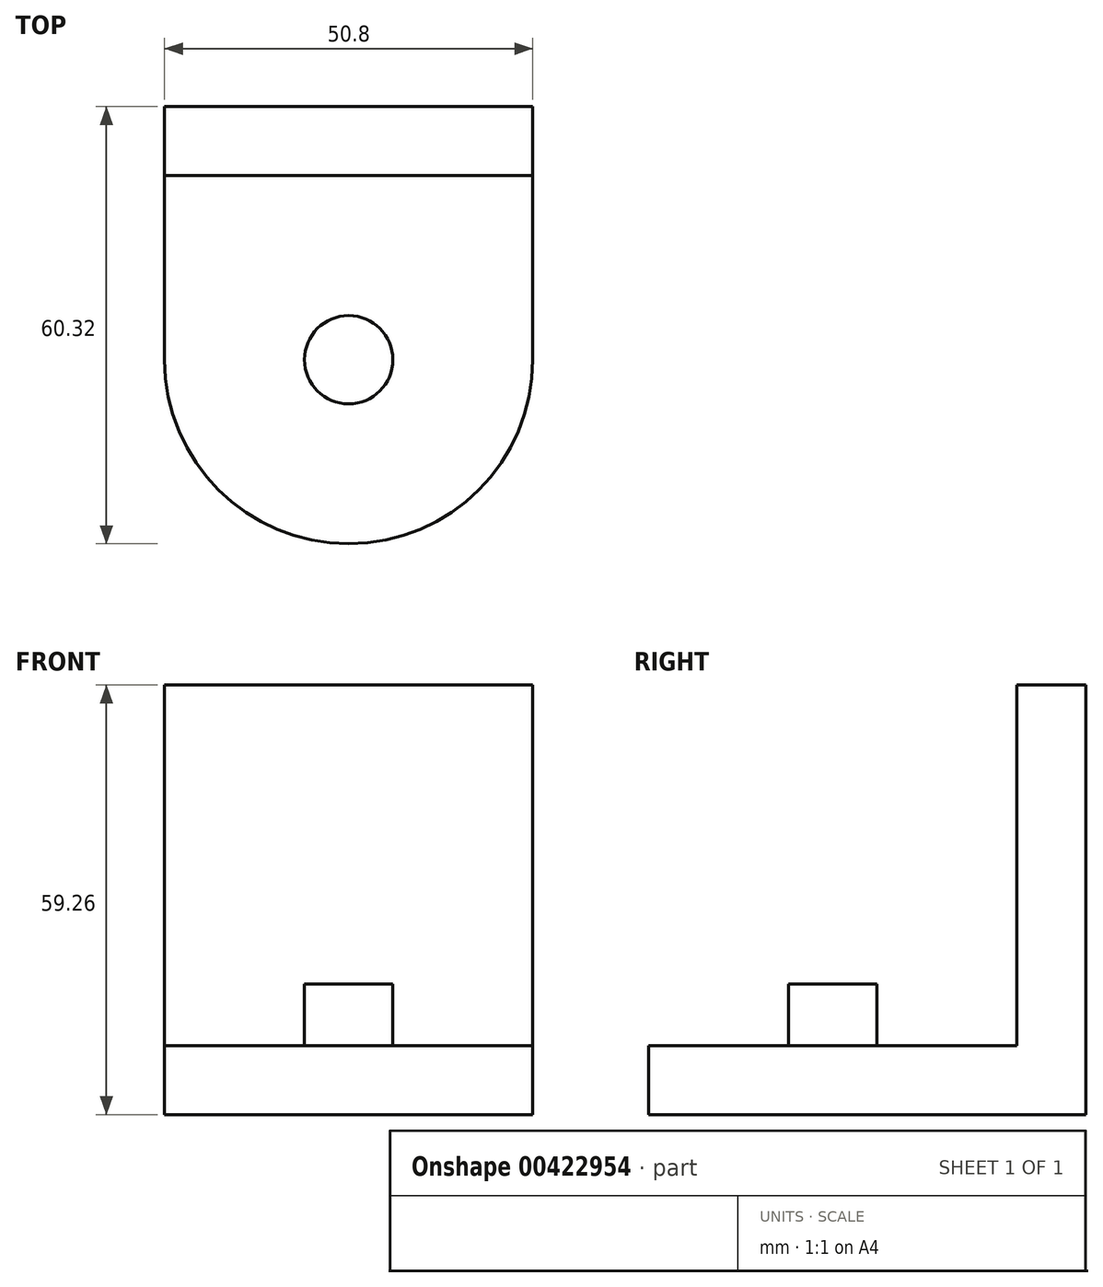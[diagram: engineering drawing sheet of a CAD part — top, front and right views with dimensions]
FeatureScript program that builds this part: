
annotation { "Feature Type Name" : "Feature", "Feature Type Description" : "" }
export const myFeature = defineFeature(function(context is Context, id is Id, definition is map)
    precondition{}
    {
        {
            var Q0;
            Q0=qCreatedBy(makeId("Top.planeOp"),FACE);
            var sketch = newSketch(context, id + "F0", { "sketchPlane" : qUnion([Q0])});
            skPoint(sketch, "E0.middle", {"position": v(0, 0) * mm});
            skLineSegment(sketch, "E1", {"start": v(-25.4, 25.4) * mm, "end": v(25.4, 25.4) * mm});
            skLineSegment(sketch, "E2", {"start": v(25.4, 25.4) * mm, "end": v(25.4, 0) * mm});
            skLineSegment(sketch, "E3", {"start": v(-25.4, 0) * mm, "end": v(-25.4, 25.4) * mm});
            skLineSegment(sketch, "E4", {"start": v(-25.4, 34.93) * mm, "end": v(25.4, 34.93) * mm});
            skLineSegment(sketch, "E5", {"start": v(25.4, 25.4) * mm, "end": v(25.4, 34.93) * mm});
            skLineSegment(sketch, "E6", {"start": v(-25.4, 34.93) * mm, "end": v(-25.4, 25.4) * mm});
            skArc(sketch, "E7", {"start": v(-25.4, 0) * mm, "mid": v(0, -25.4) * mm, "end": v(25.4, 0) * mm});
            skSolve(sketch);
        }
        {
            var Q0;
            Q0=makeQuery(id+"F0.imprint","IMPRINT",FACE,{"disambiguationData":[TD([[makeQuery(id+"F0.imprint","IMPRINT",EDGE,{"derivedFrom":sQuery(id+"F0.wireOp",EDGE,"E1")}),-1.0]])]});
            extrude(context, id + "F1", {"entities" : qUnion([Q0]), "depth" : 9.52 * mm, "offsetDistance" : 25.4 * mm});
        }
        {
            var Q0;
            Q0=makeQuery(id+"F0.imprint","IMPRINT",FACE,{"disambiguationData":[TD([[makeQuery(id+"F0.imprint","IMPRINT",EDGE,{"derivedFrom":sQuery(id+"F0.wireOp",EDGE,"E1")}),1.0]])]});
            extrude(context, id + "F2", {"entities" : qUnion([Q0]), "operationType" : NewBodyOperationType.ADD, "depth" : 59.26 * mm, "offsetDistance" : 25.4 * mm});
        }
        {
            var Q0;
            Q0=makeQuery(id+"F1.opExtrude","CAP_FACE",FACE,{"disambiguationData":[OSD([sQuery(id+"F0.wireOp",EDGE,"E1"),sQuery(id+"F0.wireOp",EDGE,"68c06d1f-53ae-42e9-a7f5-b480e38db47e"),sQuery(id+"F0.wireOp",EDGE,"E2"),sQuery(id+"F0.wireOp",EDGE,"5c3b7d94-b04e-4edd-8743-2320cabd79c5"),sQuery(id+"F0.wireOp",EDGE,"E3")])],"isStart":false});
            var sketch = newSketch(context, id + "F3", { "sketchPlane" : qUnion([Q0])});
            skCircle(sketch, "E8", {"center": v(0, 0) * mm, "radius": 6.1 * mm});
            skSolve(sketch);
        }
        {
            var Q0;
            Q0=qSketchRegion(id+"F3",true);
            extrude(context, id + "F4", {"entities" : qUnion([Q0]), "operationType" : NewBodyOperationType.ADD, "depth" : 8.46 * mm, "offsetDistance" : 25.4 * mm});
        }
    });
